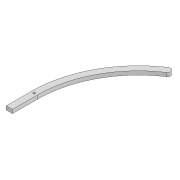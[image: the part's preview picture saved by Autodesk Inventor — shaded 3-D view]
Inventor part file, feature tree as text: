
AUTODESK INVENTOR PART (.ipt)
format: ipt  version: 2022 (Build 260153000, 153)  size: 94,208 bytes
history: native  units: mm
features: extrude x1, sketch x1
ambient origin geometry x8: Origin, YZ Plane, XZ Plane, XY Plane, X Axis, Y Axis, Z Axis, Center Point
bodies: Solid1 (feature_tree)
feature tree (2):
  extrude  "Extrusion1"  Depth=10.0mm
  sketch  "Sketch1"  dims[d0=10.0mm d1=10.0mm d3=40.0mm d4=10.0mm d6=180.0mm d7=70.0mm d8=3.3mm d9=6.0mm d10=0.0mm]
